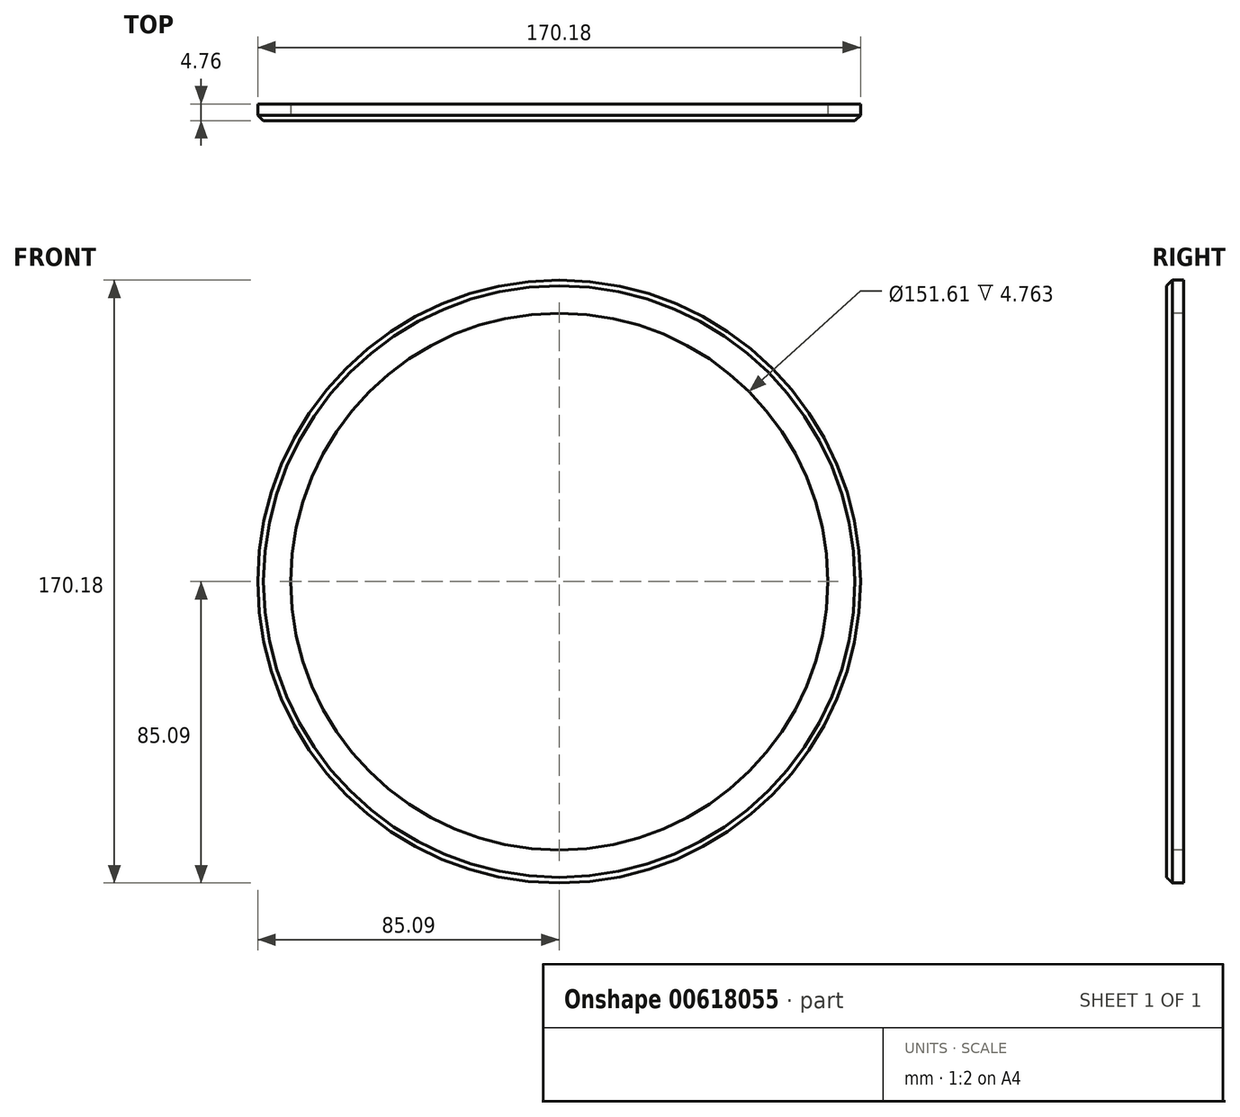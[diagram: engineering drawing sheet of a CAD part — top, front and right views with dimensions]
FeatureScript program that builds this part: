
annotation { "Feature Type Name" : "Feature", "Feature Type Description" : "" }
export const myFeature = defineFeature(function(context is Context, id is Id, definition is map)
    precondition{}
    {
        {
            var Q0;
            Q0=qCreatedBy(makeId("Front.planeOp"),FACE);
            var sketch = newSketch(context, id + "F0", { "sketchPlane" : qUnion([Q0])});
            skCircle(sketch, "E0", {"center": v(0, 0) * mm, "radius": 85.1 * mm});
            skSolve(sketch);
        }
        {
            var Q0;
            Q0=makeQuery(id+"F0.imprint","IMPRINT",FACE,{"disambiguationData":[TD([[makeQuery(id+"F0.imprint","IMPRINT",EDGE,{"derivedFrom":sQuery(id+"F0.wireOp",EDGE,"E0")}),1.0]])]});
            extrude(context, id + "F1", {"entities" : qUnion([Q0]), "depth" : 4.76 * mm, "offsetDistance" : 25.4 * mm});
        }
        {
            var Q0;
            Q0=makeQuery(id+"F1.opExtrude","CAP_FACE",FACE,{"disambiguationData":[OSD([sQuery(id+"F0.wireOp",EDGE,"E0")])],"isStart":false});
            var sketch = newSketch(context, id + "F2", { "sketchPlane" : qUnion([Q0])});
            skCircle(sketch, "E1", {"center": v(0, 0) * mm, "radius": 75.8 * mm});
            skSolve(sketch);
        }
        {
            var Q0;
            Q0=makeQuery(id+"F2.imprint","IMPRINT",FACE,{"disambiguationData":[TD([[makeQuery(id+"F2.imprint","IMPRINT",EDGE,{"derivedFrom":sQuery(id+"F2.wireOp",EDGE,"E1")}),1.0]])]});
            extrude(context, id + "F3", {"entities" : qUnion([Q0]), "operationType" : NewBodyOperationType.REMOVE, "oppositeDirection" : true, "depth" : 4.76 * mm, "offsetDistance" : 25.4 * mm});
        }
        {
            var Q0;
            Q0=makeQuery(id+"F1.opExtrude","CAP_EDGE",EDGE,{"disambiguationData":[OSD([sQuery(id+"F0.wireOp",EDGE,"E0")])],"isStart":false});
            chamfer(context, id + "F4", {"entities" : qUnion([Q0]), "width" : 1.59 * mm, "tangentPropagation" : true});
        }
    });
